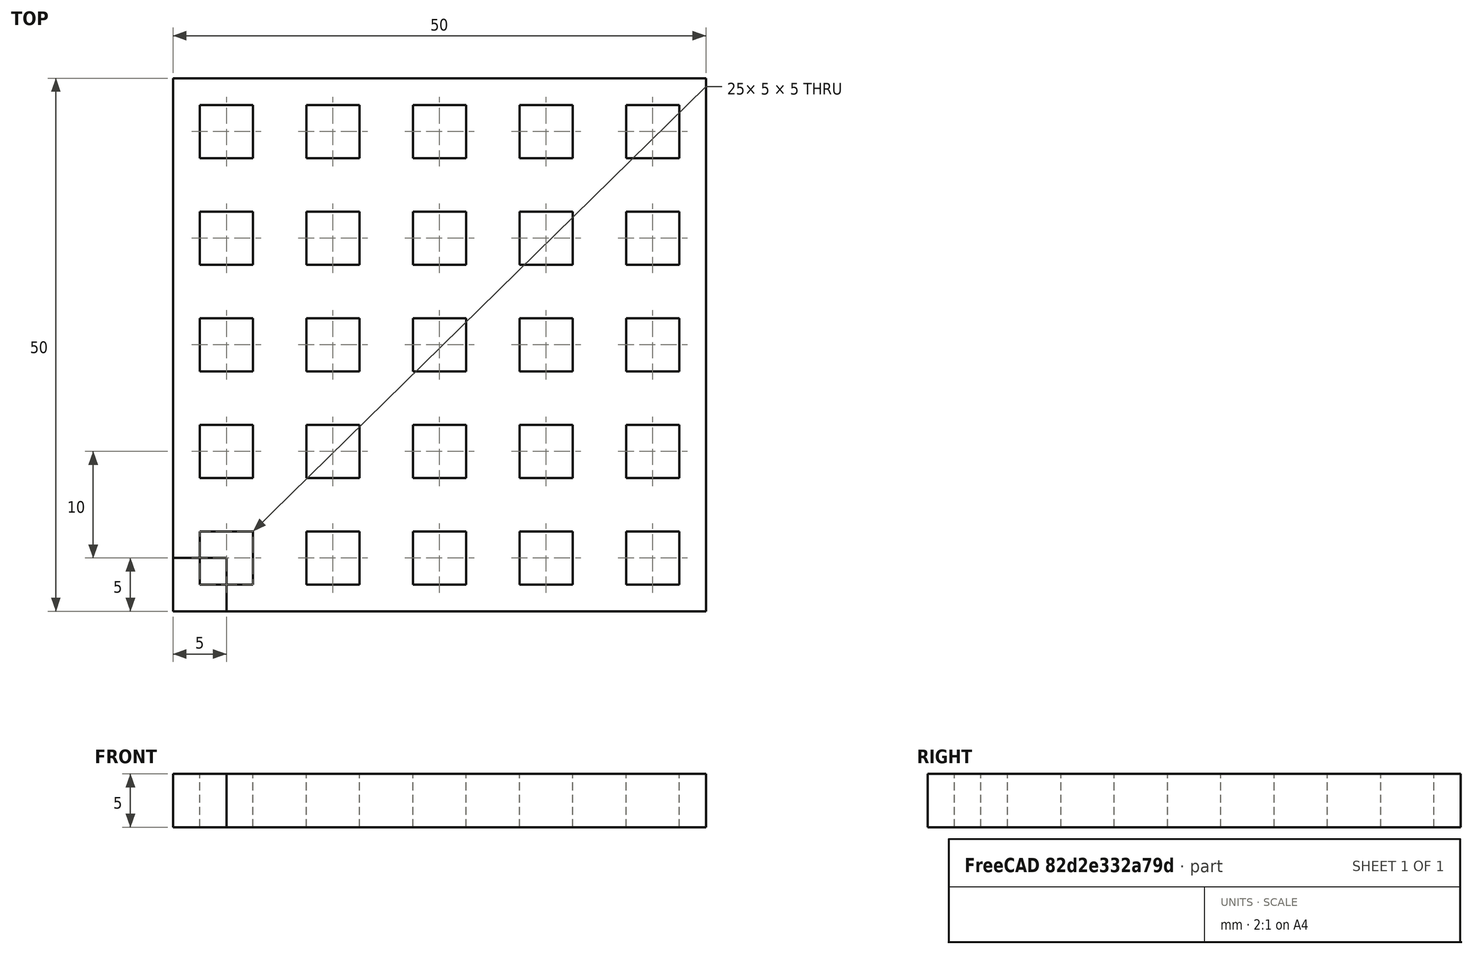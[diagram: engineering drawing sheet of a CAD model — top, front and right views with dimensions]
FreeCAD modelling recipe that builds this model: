
FCSTD DOCUMENT  (FreeCAD 0.20R29177 +426 (Git))
Label: repe
License: All rights reserved
LicenseURL: http://en.wikipedia.org/wiki/All_rights_reserved
objects: Part::Box×2, Part::FeaturePython×1, Part::Cut×1
note: 3 computed .brp shape members not serialized (recipe doc carries the construction recipe); baked Part::Feature solids carry a one-line shape summary decoded from their .brp

FEATURE [Part::Box] Box  label="Cubo"
  AttacherType = Attacher::AttachEngine3D
  Height = 5
  Length = 50
  Width = 50
FEATURE [Part::Box] Box001  label="Cubo001"
  AttacherType = Attacher::AttachEngine3D
  Height = 5
  Length = 5
  Width = 5
FEATURE [Part::FeaturePython] Array  # Draft array (typed FeaturePython)
  AlwaysSyncPlacement = false
  Angle = 360
  ArrayType = 0
  Axis = (0,0,1)
  Base = -> Box001
  Center = (0,0,0)
  Count = 25
  ExpandArray = false
  Fuse = false
  IntervalAxis = (0,0,0)
  IntervalX = (10,0,0)
  IntervalY = (0,10,0)
  IntervalZ = (0,0,100)
  NumberCircles = 3
  NumberPolar = 5
  NumberX = 5
  NumberY = 5
  NumberZ = 1
  Placement = pos=(2.5,2.5,0) rot=(0,0,1;0rad)
  PlacementList = 25 placements: [(0,0,0),(0,10,0),(0,20,0),(0,30,0),(0,40,0),(10,0,0),(10,10,0),(10,20,0),(10,30,0),(10,40,0),(20,0,0),(20,10,0),(20,20,0),(20,30,0),(20,40,0),(30,0,0),(30,10,0),(30,20,0),(30,30,0),(30,40,0),(40,0,0),(40,10,0),(40,20,0),(40,30,0),(40,40,0)]
  RadialDistance = 50
  ScaleList = (25) [(1,1,1),(1,1,1),(1,1,1),(1,1,1),(1,1,1),(1,1,1),(1,1,1),(1,1,1),(1,1,1),(1,1,1),(1,1,1),(1,1,1),(1,1,1),(1,1,1),(1,1,1),(1,1,1),(1,1,1),(1,1,1),+7 more]
  Symmetry = 1
  TangentialDistance = 25
FEATURE [Part::Cut] Cut
  Base = -> Box
  Refine = true
  Tool = -> Array
